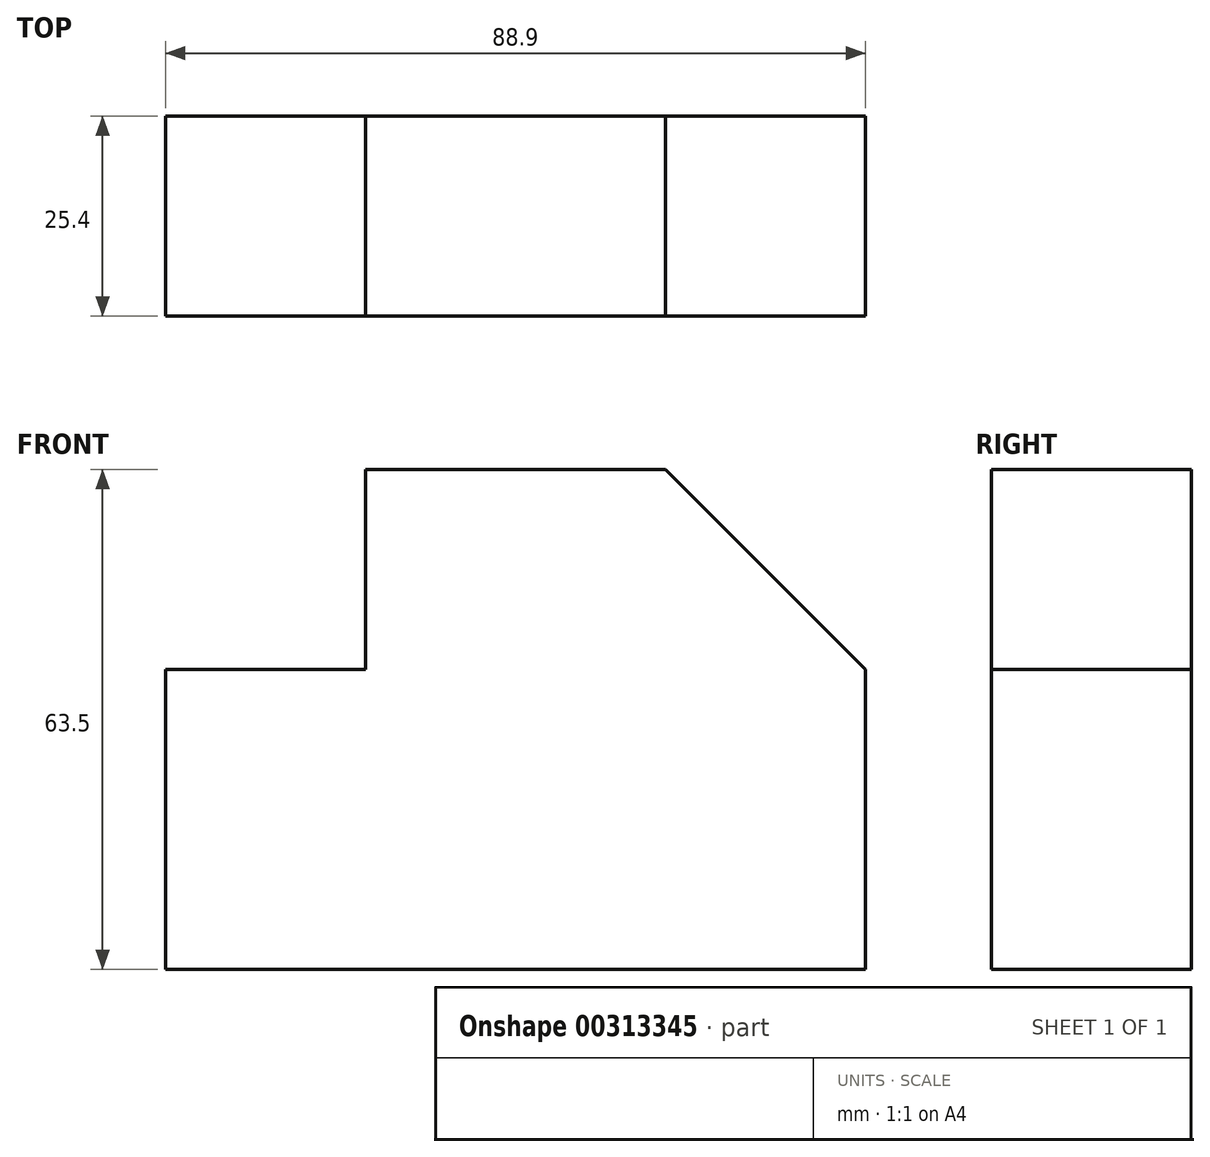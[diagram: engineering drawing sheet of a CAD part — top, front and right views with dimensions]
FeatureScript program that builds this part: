
annotation { "Feature Type Name" : "Feature", "Feature Type Description" : "" }
export const myFeature = defineFeature(function(context is Context, id is Id, definition is map)
    precondition{}
    {
        {
            var Q0;
            Q0=qCreatedBy(makeId("Front.planeOp"),FACE);
            var sketch = newSketch(context, id + "F0", { "sketchPlane" : qUnion([Q0])});
            skLineSegment(sketch, "E0", {"start": v(-38.88, -50.6) * mm, "end": v(50.02, -50.6) * mm});
            skLineSegment(sketch, "E1", {"start": v(-38.88, -50.6) * mm, "end": v(-38.88, -12.5) * mm});
            skLineSegment(sketch, "E2", {"start": v(-38.88, -12.5) * mm, "end": v(-13.48, -12.5) * mm});
            skLineSegment(sketch, "E3", {"start": v(-13.48, -12.5) * mm, "end": v(-13.48, 12.9) * mm});
            skLineSegment(sketch, "E4", {"start": v(-13.48, 12.9) * mm, "end": v(24.62, 12.9) * mm});
            skLineSegment(sketch, "E5", {"start": v(50.02, -50.6) * mm, "end": v(50.02, -12.5) * mm});
            skLineSegment(sketch, "E6", {"start": v(50.02, -12.5) * mm, "end": v(24.62, 12.9) * mm});
            skSolve(sketch);
        }
        {
            var Q0;
            Q0=makeQuery(id+"F0.imprint","IMPRINT",FACE,{"disambiguationData":[TD([[makeQuery(id+"F0.imprint","IMPRINT",EDGE,{"derivedFrom":sQuery(id+"F0.wireOp",EDGE,"E0")}),1.0]])]});
            extrude(context, id + "F1", {"entities" : qUnion([Q0]), "depth" : 25.4 * mm});
        }
    });
